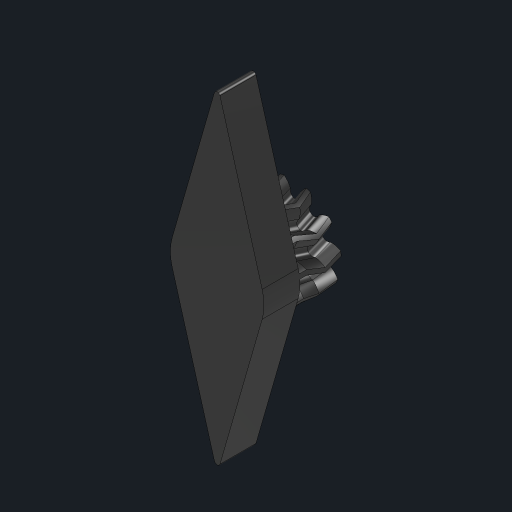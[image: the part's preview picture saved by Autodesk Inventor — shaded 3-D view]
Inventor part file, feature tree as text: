
AUTODESK INVENTOR PART (.ipt)
format: ipt  version: 2023.2 (Build 272271030, 271C)  size: 5,978,624 bytes
history: native  units: mm
features: sketch x4, extrude x4, projected_geometry x3, helix x1, pattern_circular x1, mirror x1, fillet x1
ambient origin geometry x8: Origin, YZ Plane, XZ Plane, XY Plane, X Axis, Y Axis, Z Axis, Center Point
bodies: Solid1 (feature_tree)
feature tree (15):
  sketch  "Sketch1"  dims[d0=2.5mm d1=0.0mm]
  extrude  "Extrusion1"  Depth=10.0mm TaperAngle=0.0deg
  helix  "Coil1"  [1 undecoded]
  pattern_circular  "Circular Pattern1"  [2 undecoded]
  mirror  "Mirror1"
  extrude  "Extrusion2"  [1 undecoded]
  extrude  "Extrusion3"  [1 undecoded]
  fillet  "Fillet1"  [1 undecoded]
  extrude  "Extrusion4"  [1 undecoded]
  sketch  "Sketch2"  dims[d2=110.1mm d3=10.0mm d4=10.0mm d5=0.0mm d6=90.0deg d7=90.0deg d8=0.0mm d9=0.0mm d10=110.0mm d11=360.0deg d13=1.0mm d14=0.0mm d15=47.0mm]
  projected_geometry  "Projected Loop1"
  sketch  "Sketch3"  dims[d16=5.0mm d17=0.0mm]
  projected_geometry  "Projected Loop2"
  sketch  "Sketch4"  dims[d18=0.4mm d19=0.25mm d20=0.0mm]
  projected_geometry  "Projected Loop3"
note: 7 required parameter values undecoded (feature->parameter linkage not recoverable at this tier; creation-order binding heuristic only, values carry confidence <= 0.55)
